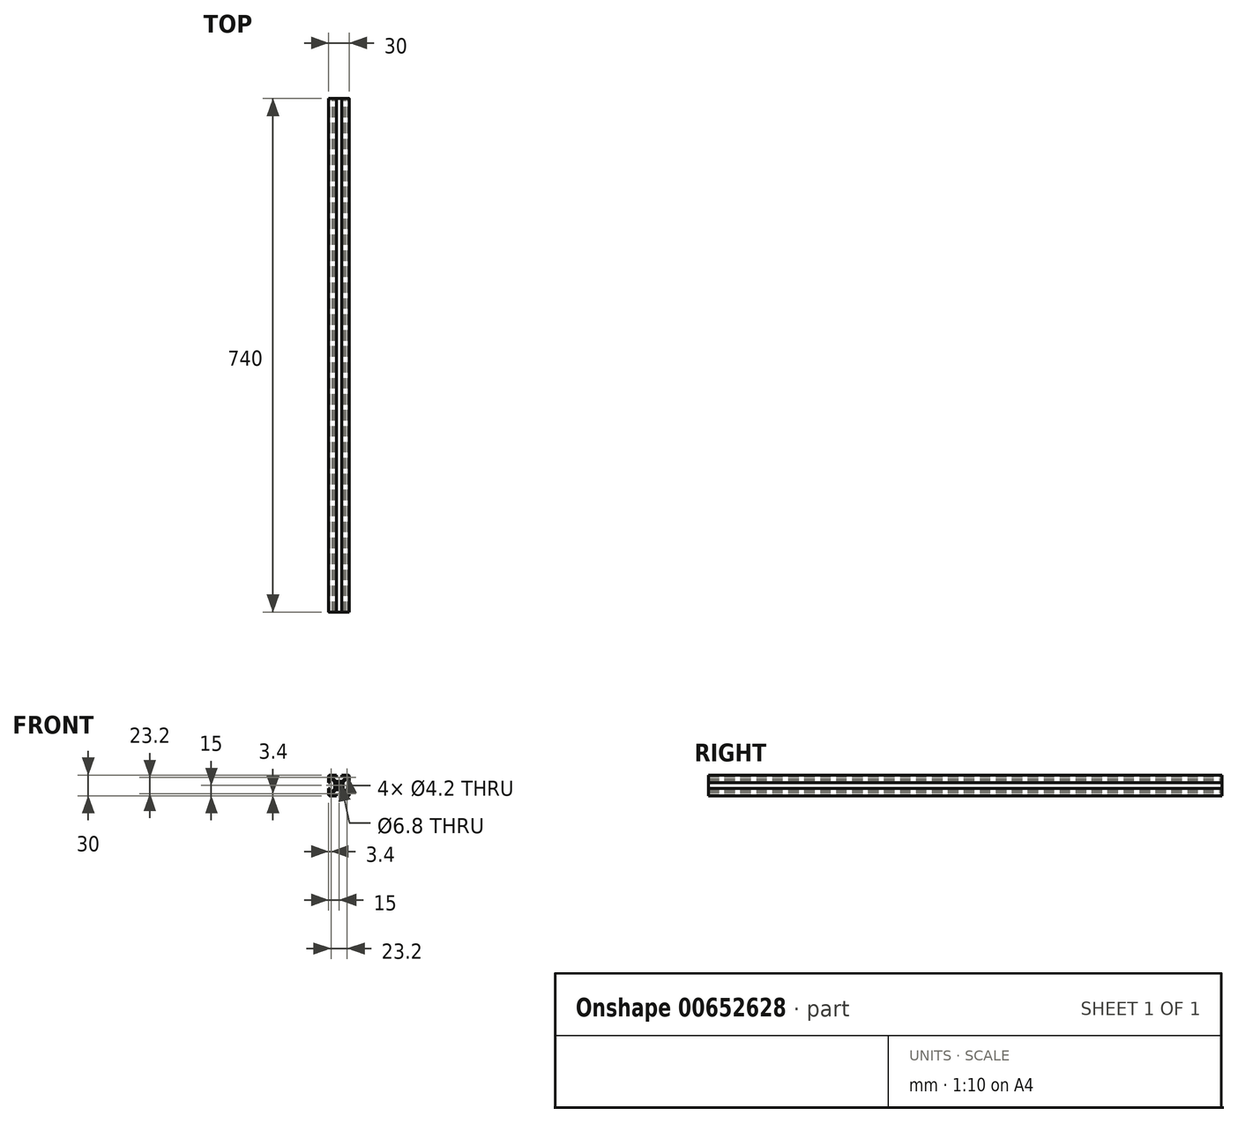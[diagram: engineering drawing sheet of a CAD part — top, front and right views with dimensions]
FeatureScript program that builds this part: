
annotation { "Feature Type Name" : "Feature", "Feature Type Description" : "" }
export const myFeature = defineFeature(function(context is Context, id is Id, definition is map)
    precondition{}
    {
        {
            var Q0;
            Q0=qCreatedBy(makeId("Front.planeOp"),FACE);
            var sketch = newSketch(context, id + "F0", { "sketchPlane" : qUnion([Q0])});
            skLineSegment(sketch, "E0", {"start": v(0, 6) * mm, "end": v(-4.59, 6) * mm});
            skLineSegment(sketch, "E1", {"start": v(-4.59, 6) * mm, "end": v(-8.25, 9.66) * mm});
            skLineSegment(sketch, "E2", {"start": v(-8.25, 9.66) * mm, "end": v(-8.25, 13) * mm});
            skLineSegment(sketch, "E3", {"start": v(-8.25, 13) * mm, "end": v(-4, 13) * mm});
            skLineSegment(sketch, "E4", {"start": v(-4, 13) * mm, "end": v(-4, 15) * mm});
            skLineSegment(sketch, "E5", {"start": v(-4, 15) * mm, "end": v(-13, 15) * mm});
            skLineSegment(sketch, "E6", {"start": v(-15, 13) * mm, "end": v(-15, 4) * mm});
            skLineSegment(sketch, "E7", {"start": v(-15, 4) * mm, "end": v(-13, 4) * mm});
            skLineSegment(sketch, "E8", {"start": v(-13, 4) * mm, "end": v(-13, 8.25) * mm});
            skLineSegment(sketch, "E9", {"start": v(-13, 8.25) * mm, "end": v(-9.66, 8.25) * mm});
            skLineSegment(sketch, "E10", {"start": v(-9.66, 8.25) * mm, "end": v(-6, 4.59) * mm});
            skLineSegment(sketch, "E11", {"start": v(-6, 4.59) * mm, "end": v(-6, 0) * mm});
            skLineSegment(sketch, "E12", {"start": v(-6, 0) * mm, "end": v(0, 0) * mm, "construction": true});
            skLineSegment(sketch, "E13", {"start": v(0, 0) * mm, "end": v(0, 6) * mm, "construction": true});
            skArc(sketch, "E14", {"start": v(0, 3.4) * mm, "mid": v(-2.4, 2.4) * mm, "end": v(-3.4, 0) * mm});
            skCircle(sketch, "E15", {"center": v(-11.6, 11.6) * mm, "radius": 2.1 * mm});
            skLineSegment(sketch, "E16", {"start": v(0, 0) * mm, "end": v(-7.38, 7.38) * mm, "construction": true});
            skLineSegment(sketch, "E17.1.0", {"start": v(-8.25, -13) * mm, "end": v(-8.25, -9.66) * mm});
            skLineSegment(sketch, "E17.1.1", {"start": v(-4, -15) * mm, "end": v(-4, -13) * mm});
            skLineSegment(sketch, "E17.1.2", {"start": v(-4, -13) * mm, "end": v(-8.25, -13) * mm});
            skLineSegment(sketch, "E17.1.3", {"start": v(-15, -4) * mm, "end": v(-15, -13) * mm});
            skLineSegment(sketch, "E17.1.4", {"start": v(-8.25, -9.66) * mm, "end": v(-4.59, -6) * mm});
            skLineSegment(sketch, "E17.1.5", {"start": v(-13, -15) * mm, "end": v(-4, -15) * mm});
            skLineSegment(sketch, "E17.1.6", {"start": v(-4.59, -6) * mm, "end": v(0, -6) * mm});
            skLineSegment(sketch, "E17.1.7", {"start": v(0, -6) * mm, "end": v(0, 0) * mm, "construction": true});
            skLineSegment(sketch, "E17.1.8", {"start": v(0, 0) * mm, "end": v(-6, 0) * mm, "construction": true});
            skLineSegment(sketch, "E17.1.9", {"start": v(-13, -4) * mm, "end": v(-15, -4) * mm});
            skLineSegment(sketch, "E17.1.10", {"start": v(-13, -8.25) * mm, "end": v(-13, -4) * mm});
            skArc(sketch, "E17.1.11", {"start": v(-3.4, 0) * mm, "mid": v(-2.4, -2.4) * mm, "end": v(0, -3.4) * mm});
            skLineSegment(sketch, "E17.1.12", {"start": v(-9.66, -8.25) * mm, "end": v(-13, -8.25) * mm});
            skLineSegment(sketch, "E17.1.13", {"start": v(0, 0) * mm, "end": v(-7.38, -7.38) * mm, "construction": true});
            skLineSegment(sketch, "E17.1.14", {"start": v(-6, -4.59) * mm, "end": v(-9.66, -8.25) * mm});
            skCircle(sketch, "E17.1.15", {"center": v(-11.6, -11.6) * mm, "radius": 2.1 * mm});
            skLineSegment(sketch, "E17.1.16", {"start": v(-6, 0) * mm, "end": v(-6, -4.59) * mm});
            skLineSegment(sketch, "E17.2.0", {"start": v(13, -8.25) * mm, "end": v(9.66, -8.25) * mm});
            skLineSegment(sketch, "E17.2.1", {"start": v(15, -4) * mm, "end": v(13, -4) * mm});
            skLineSegment(sketch, "E17.2.2", {"start": v(13, -4) * mm, "end": v(13, -8.25) * mm});
            skLineSegment(sketch, "E17.2.3", {"start": v(4, -15) * mm, "end": v(13, -15) * mm});
            skLineSegment(sketch, "E17.2.4", {"start": v(9.66, -8.25) * mm, "end": v(6, -4.59) * mm});
            skLineSegment(sketch, "E17.2.5", {"start": v(15, -13) * mm, "end": v(15, -4) * mm});
            skLineSegment(sketch, "E17.2.6", {"start": v(6, -4.59) * mm, "end": v(6, 0) * mm});
            skLineSegment(sketch, "E17.2.7", {"start": v(6, 0) * mm, "end": v(0, 0) * mm, "construction": true});
            skLineSegment(sketch, "E17.2.8", {"start": v(0, 0) * mm, "end": v(0, -6) * mm, "construction": true});
            skLineSegment(sketch, "E17.2.9", {"start": v(4, -13) * mm, "end": v(4, -15) * mm});
            skLineSegment(sketch, "E17.2.10", {"start": v(8.25, -13) * mm, "end": v(4, -13) * mm});
            skArc(sketch, "E17.2.11", {"start": v(0, -3.4) * mm, "mid": v(2.4, -2.4) * mm, "end": v(3.4, 0) * mm});
            skLineSegment(sketch, "E17.2.12", {"start": v(8.25, -9.66) * mm, "end": v(8.25, -13) * mm});
            skLineSegment(sketch, "E17.2.13", {"start": v(0, 0) * mm, "end": v(7.38, -7.38) * mm, "construction": true});
            skLineSegment(sketch, "E17.2.14", {"start": v(4.59, -6) * mm, "end": v(8.25, -9.66) * mm});
            skCircle(sketch, "E17.2.15", {"center": v(11.6, -11.6) * mm, "radius": 2.1 * mm});
            skLineSegment(sketch, "E17.2.16", {"start": v(0, -6) * mm, "end": v(4.59, -6) * mm});
            skLineSegment(sketch, "E17.3.0", {"start": v(8.25, 13) * mm, "end": v(8.25, 9.66) * mm});
            skLineSegment(sketch, "E17.3.1", {"start": v(4, 15) * mm, "end": v(4, 13) * mm});
            skLineSegment(sketch, "E17.3.2", {"start": v(4, 13) * mm, "end": v(8.25, 13) * mm});
            skLineSegment(sketch, "E17.3.3", {"start": v(15, 4) * mm, "end": v(15, 13) * mm});
            skLineSegment(sketch, "E17.3.4", {"start": v(8.25, 9.66) * mm, "end": v(4.59, 6) * mm});
            skLineSegment(sketch, "E17.3.5", {"start": v(13, 15) * mm, "end": v(4, 15) * mm});
            skLineSegment(sketch, "E17.3.6", {"start": v(4.59, 6) * mm, "end": v(0, 6) * mm});
            skLineSegment(sketch, "E17.3.7", {"start": v(0, 6) * mm, "end": v(0, 0) * mm, "construction": true});
            skLineSegment(sketch, "E17.3.8", {"start": v(0, 0) * mm, "end": v(6, 0) * mm, "construction": true});
            skLineSegment(sketch, "E17.3.9", {"start": v(13, 4) * mm, "end": v(15, 4) * mm});
            skLineSegment(sketch, "E17.3.10", {"start": v(13, 8.25) * mm, "end": v(13, 4) * mm});
            skArc(sketch, "E17.3.11", {"start": v(3.4, 0) * mm, "mid": v(2.4, 2.4) * mm, "end": v(0, 3.4) * mm});
            skLineSegment(sketch, "E17.3.12", {"start": v(9.66, 8.25) * mm, "end": v(13, 8.25) * mm});
            skLineSegment(sketch, "E17.3.13", {"start": v(0, 0) * mm, "end": v(7.38, 7.38) * mm, "construction": true});
            skLineSegment(sketch, "E17.3.14", {"start": v(6, 4.59) * mm, "end": v(9.66, 8.25) * mm});
            skCircle(sketch, "E17.3.15", {"center": v(11.6, 11.6) * mm, "radius": 2.1 * mm});
            skLineSegment(sketch, "E17.3.16", {"start": v(6, 0) * mm, "end": v(6, 4.59) * mm});
            skPoint(sketch, "E18.visualSharp", {"position": v(-15, 15) * mm});
            skArc(sketch, "E18.filletArc", {"start": v(-13, 15) * mm, "mid": v(-14.41, 14.41) * mm, "end": v(-15, 13) * mm});
            skPoint(sketch, "E19.visualSharp", {"position": v(15, 15) * mm});
            skArc(sketch, "E19.filletArc", {"start": v(15, 13) * mm, "mid": v(14.41, 14.41) * mm, "end": v(13, 15) * mm});
            skPoint(sketch, "E20.visualSharp", {"position": v(15, -15) * mm});
            skArc(sketch, "E20.filletArc", {"start": v(13, -15) * mm, "mid": v(14.41, -14.41) * mm, "end": v(15, -13) * mm});
            skPoint(sketch, "E21.visualSharp", {"position": v(-15, -15) * mm});
            skArc(sketch, "E21.filletArc", {"start": v(-15, -13) * mm, "mid": v(-14.41, -14.41) * mm, "end": v(-13, -15) * mm});
            skSolve(sketch);
        }
        {
            var Q0;
            Q0 = qSketchRegion(id + "F0", true);
            extrude(context, id + "F1", {"entities" : qUnion([Q0]), "depth" : 740 * mm, "offsetDistance" : 25 * mm});
        }
    });
